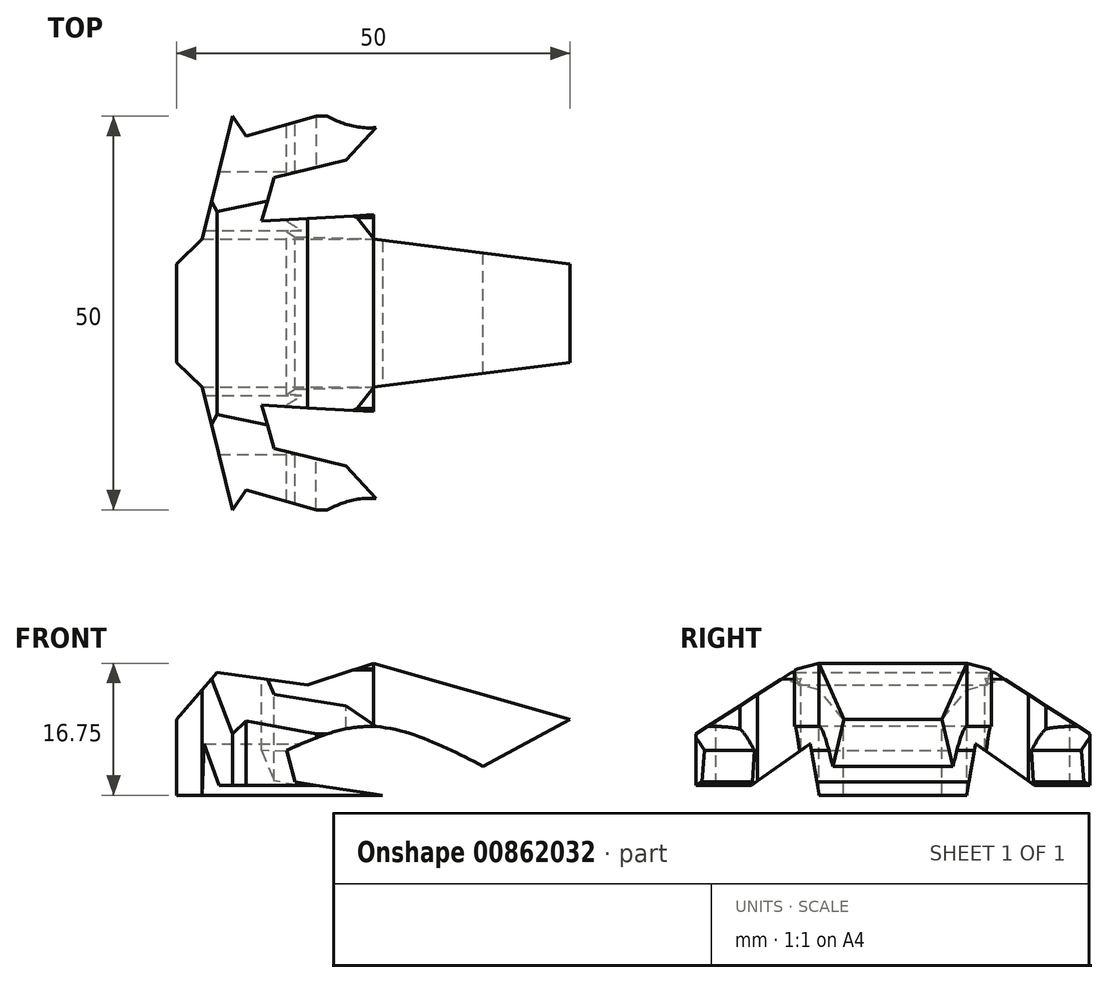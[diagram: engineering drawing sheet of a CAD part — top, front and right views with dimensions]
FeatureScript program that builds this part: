
annotation { "Feature Type Name" : "Feature", "Feature Type Description" : "" }
export const myFeature = defineFeature(function(context is Context, id is Id, definition is map)
    precondition{}
    {
        {
            var Q0;
            Q0=qCreatedBy(makeId("Top.planeOp"),FACE);
            var sketch = newSketch(context, id + "F0", { "sketchPlane" : qUnion([Q0])});
            skLineSegment(sketch, "E0.bottom", {"start": v(25, -25) * mm, "end": v(-25, -25) * mm});
            skLineSegment(sketch, "E0.top", {"start": v(25, 25) * mm, "end": v(-25, 25) * mm});
            skLineSegment(sketch, "E0.left", {"start": v(25, -25) * mm, "end": v(25, 25) * mm});
            skLineSegment(sketch, "E0.right", {"start": v(-25, -25) * mm, "end": v(-25, 25) * mm});
            skPoint(sketch, "E0.middle", {"position": v(0, 0) * mm});
            skSolve(sketch);
        }
        {
            var Q0;
            Q0=makeQuery(id+"F0.imprint","IMPRINT",FACE,{"disambiguationData":[TD([[makeQuery(id+"F0.imprint","IMPRINT",EDGE,{"derivedFrom":sQuery(id+"F0.wireOp",EDGE,"E0.bottom")}),-1.0]])]});
            extrude(context, id + "F1", {"entities" : qUnion([Q0]), "depth" : 50 * mm, "offsetDistance" : 25 * mm});
        }
        {
            var Q0;
            Q0=makeQuery(id+"F1.opExtrude","SWEPT_FACE",FACE,{"disambiguationData":[OSD([sQuery(id+"F0.wireOp",EDGE,"E0.top")])]});
            var sketch = newSketch(context, id + "F2", { "sketchPlane" : qUnion([Q0])});
            skLineSegment(sketch, "E1", {"start": v(-25, 25) * mm, "end": v(0, 32.14) * mm});
            skPoint(sketch, "E2", {"position": v(0, 0) * mm});
            skFitSpline(sketch, "E3", {"points": [v(-13.92, 19.08) * mm, v(0, 24.12) * mm, v(11, 21.1) * mm], "startDerivative": vector(26.84, 13.7) * mm, "endDerivative": vector(22.91, -10.19) * mm});
            skLineSegment(sketch, "E4", {"start": v(-25, 25) * mm, "end": v(-13.92, 19.08) * mm});
            skLineSegment(sketch, "E5", {"start": v(0, 32.14) * mm, "end": v(8.38, 29.43) * mm});
            skLineSegment(sketch, "E6", {"start": v(8.38, 29.43) * mm, "end": v(19.86, 30.97) * mm});
            skLineSegment(sketch, "E7", {"start": v(11, 21.1) * mm, "end": v(9.92, 17.07) * mm});
            skLineSegment(sketch, "E8", {"start": v(9.92, 17.07) * mm, "end": v(-1.63, 15.32) * mm});
            skLineSegment(sketch, "E9", {"start": v(-1.63, 15.32) * mm, "end": v(25, 15.32) * mm});
            skLineSegment(sketch, "E10", {"start": v(25, 15.32) * mm, "end": v(25, 25) * mm});
            skLineSegment(sketch, "E11", {"start": v(25, 25) * mm, "end": v(19.86, 30.97) * mm});
            skSolve(sketch);
        }
        {
            var Q0;
            Q0=makeQuery(id+"F1.opExtrude","SWEPT_FACE",FACE,{"disambiguationData":[OSD([sQuery(id+"F0.wireOp",EDGE,"E0.left")])]});
            var sketch = newSketch(context, id + "F3", { "sketchPlane" : qUnion([Q0])});
            skLineSegment(sketch, "E12", {"start": v(-25, 23.18) * mm, "end": v(-10.92, 26.77) * mm});
            skLineSegment(sketch, "E13", {"start": v(-25, 16.67) * mm, "end": v(-17.95, 16.67) * mm});
            skLineSegment(sketch, "E14", {"start": v(-17.95, 16.67) * mm, "end": v(-10.5, 21.93) * mm});
            skLineSegment(sketch, "E15", {"start": v(-10.5, 21.93) * mm, "end": v(-9.38, 15.39) * mm});
            skLineSegment(sketch, "E16", {"start": v(-9.38, 15.39) * mm, "end": v(0, 15.39) * mm});
            skLineSegment(sketch, "E17", {"start": v(-10.92, 26.77) * mm, "end": v(-12.11, 31.46) * mm});
            skLineSegment(sketch, "E18", {"start": v(-12.11, 31.46) * mm, "end": v(-6.5, 32.9) * mm});
            skLineSegment(sketch, "E19", {"start": v(-25, 23.18) * mm, "end": v(-12.11, 31.46) * mm});
            skLineSegment(sketch, "E20", {"start": v(-10.92, 26.77) * mm, "end": v(0, 32.9) * mm});
            skLineSegment(sketch, "E21", {"start": v(0, 32.9) * mm, "end": v(-6.5, 32.9) * mm});
            skLineSegment(sketch, "E22.MirrorCS", {"start": v(0, 32.9) * mm, "end": v(6.5, 32.9) * mm});
            skLineSegment(sketch, "E23.MirrorCS", {"start": v(12.11, 31.46) * mm, "end": v(6.5, 32.9) * mm});
            skLineSegment(sketch, "E24.MirrorCS", {"start": v(10.92, 26.77) * mm, "end": v(0, 32.9) * mm});
            skLineSegment(sketch, "E25.MirrorCS", {"start": v(10.92, 26.77) * mm, "end": v(12.11, 31.46) * mm});
            skLineSegment(sketch, "E26.MirrorCS", {"start": v(25, 23.18) * mm, "end": v(12.11, 31.46) * mm});
            skLineSegment(sketch, "E27.MirrorCS", {"start": v(25, 23.18) * mm, "end": v(10.92, 26.77) * mm});
            skLineSegment(sketch, "E28.MirrorCS", {"start": v(17.95, 16.67) * mm, "end": v(10.5, 21.93) * mm});
            skLineSegment(sketch, "E29.MirrorCS", {"start": v(25, 16.67) * mm, "end": v(17.95, 16.67) * mm});
            skLineSegment(sketch, "E30.MirrorCS", {"start": v(10.5, 21.93) * mm, "end": v(9.38, 15.39) * mm});
            skLineSegment(sketch, "E31.MirrorCS", {"start": v(9.38, 15.39) * mm, "end": v(0, 15.39) * mm});
            skLineSegment(sketch, "E32", {"start": v(-25, 23.18) * mm, "end": v(-25, 16.67) * mm});
            skLineSegment(sketch, "E33", {"start": v(25, 23.18) * mm, "end": v(25, 16.67) * mm});
            skLineSegment(sketch, "E34", {"start": v(-5.46, 29.83) * mm, "end": v(5.46, 29.83) * mm});
            skSolve(sketch);
        }
        {
            var Q0;
            Q0=makeQuery(id+"F1.opExtrude","CAP_FACE",FACE,{"disambiguationData":[OSD([sQuery(id+"F0.wireOp",EDGE,"E0.bottom"),sQuery(id+"F0.wireOp",EDGE,"E0.top"),sQuery(id+"F0.wireOp",EDGE,"E0.left"),sQuery(id+"F0.wireOp",EDGE,"E0.right")])],"isStart":false});
            var sketch = newSketch(context, id + "F4", { "sketchPlane" : qUnion([Q0])});
            skLineSegment(sketch, "E35", {"start": v(0, -9.38) * mm, "end": v(25, -6.25) * mm});
            skLineSegment(sketch, "E36", {"start": v(0, 9.38) * mm, "end": v(25, 6.25) * mm});
            skLineSegment(sketch, "E37", {"start": v(-17.85, -25) * mm, "end": v(-21.77, -9.37) * mm});
            skLineSegment(sketch, "E38", {"start": v(-25, 0) * mm, "end": v(25, 0) * mm});
            skLineSegment(sketch, "E39", {"start": v(-12.58, -17.21) * mm, "end": v(-14.18, -11.7) * mm});
            skLineSegment(sketch, "E40", {"start": v(-14.18, -11.7) * mm, "end": v(0, -12.5) * mm});
            skLineSegment(sketch, "E41", {"start": v(-16.14, -22.48) * mm, "end": v(-7.23, -25) * mm});
            skLineSegment(sketch, "E42", {"start": v(-7.23, -25) * mm, "end": v(1.64, -25) * mm});
            skLineSegment(sketch, "E43", {"start": v(-12.58, -17.21) * mm, "end": v(-3.47, -19.45) * mm});
            skLineSegment(sketch, "E44", {"start": v(-3.47, -19.45) * mm, "end": v(1.64, -25) * mm});
            skLineSegment(sketch, "E45.MirrorCS", {"start": v(-17.85, 25) * mm, "end": v(-21.77, 9.37) * mm});
            skLineSegment(sketch, "E46.MirrorCS", {"start": v(-12.58, 17.21) * mm, "end": v(-14.18, 11.7) * mm});
            skLineSegment(sketch, "E47.MirrorCS", {"start": v(-14.18, 11.7) * mm, "end": v(0, 12.5) * mm});
            skLineSegment(sketch, "E48.MirrorCS", {"start": v(-12.58, 17.21) * mm, "end": v(-3.47, 19.45) * mm});
            skLineSegment(sketch, "E49.MirrorCS", {"start": v(-16.14, 22.48) * mm, "end": v(-7.23, 25) * mm});
            skLineSegment(sketch, "E50.MirrorCS", {"start": v(-3.47, 19.45) * mm, "end": v(1.64, 25) * mm});
            skLineSegment(sketch, "E51.MirrorCS", {"start": v(-7.23, 25) * mm, "end": v(1.64, 25) * mm});
            skLineSegment(sketch, "E52", {"start": v(-21.77, -9.37) * mm, "end": v(-25, -6.25) * mm});
            skLineSegment(sketch, "E53", {"start": v(-25, -6.25) * mm, "end": v(-25, 0) * mm});
            skLineSegment(sketch, "E54.MirrorCS", {"start": v(-25, 6.25) * mm, "end": v(-25, 0) * mm});
            skLineSegment(sketch, "E55.MirrorCS", {"start": v(-21.77, 9.37) * mm, "end": v(-25, 6.25) * mm});
            skLineSegment(sketch, "E56", {"start": v(0, -12.5) * mm, "end": v(0, -9.38) * mm});
            skLineSegment(sketch, "E57", {"start": v(0, 9.38) * mm, "end": v(0, 12.5) * mm});
            skLineSegment(sketch, "E58", {"start": v(-17.85, -25) * mm, "end": v(-16.14, -22.48) * mm});
            skLineSegment(sketch, "E59", {"start": v(-17.85, 25) * mm, "end": v(-16.14, 22.48) * mm});
            skLineSegment(sketch, "E60", {"start": v(25, -6.25) * mm, "end": v(25, 6.25) * mm});
            skSolve(sketch);
        }
        {
            var Q0;
            {var subQ0=sQuery(id+"F4.wireOp",EDGE,"E37");Q0=makeQuery(id+"F4.imprint","IMPRINT",FACE,{"disambiguationData":[TD([[makeQuery(id+"F4.imprint","IMPRINT",EDGE,{"derivedFrom":subQ0}),1.0]])]});}
            var Q1;
            {var subQ0=sQuery(id+"F4.wireOp",EDGE,"E41");Q1=makeQuery(id+"F4.imprint","IMPRINT",FACE,{"disambiguationData":[TD([[makeQuery(id+"F4.imprint","IMPRINT",EDGE,{"derivedFrom":subQ0}),-1.0]])]});}
            var Q2;
            {var subQ0=sQuery(id+"F4.wireOp",EDGE,"E45.MirrorCS");Q2=makeQuery(id+"F4.imprint","IMPRINT",FACE,{"disambiguationData":[TD([[makeQuery(id+"F4.imprint","IMPRINT",EDGE,{"derivedFrom":subQ0}),-1.0]])]});}
            var Q3;
            {var subQ0=sQuery(id+"F4.wireOp",EDGE,"E49.MirrorCS");Q3=makeQuery(id+"F4.imprint","IMPRINT",FACE,{"disambiguationData":[TD([[makeQuery(id+"F4.imprint","IMPRINT",EDGE,{"derivedFrom":subQ0}),1.0]])]});}
            var Q4;
            {var subQ0=sQuery(id+"F4.wireOp",EDGE,"E36");Q4=makeQuery(id+"F4.imprint","IMPRINT",FACE,{"disambiguationData":[TD([[makeQuery(id+"F4.imprint","IMPRINT",EDGE,{"derivedFrom":subQ0}),1.0]])]});}
            var Q5;
            {var subQ4=sQuery(id+"F4.wireOp",EDGE,"E35");Q5=makeQuery(id+"F4.imprint","IMPRINT",FACE,{"disambiguationData":[TD([[makeQuery(id+"F4.imprint","IMPRINT",EDGE,{"derivedFrom":subQ4}),-1.0]])]});}
            extrude(context, id + "F5", {"entities" : qUnion([Q0, Q1, Q2, Q3, Q4, Q5]), "operationType" : NewBodyOperationType.REMOVE, "oppositeDirection" : true, "depth" : 50 * mm, "offsetDistance" : 25 * mm});
        }
        {
            var Q0;
            {var subQ4=sQuery(id+"F2.wireOp",EDGE,"E1");Q0=makeQuery(id+"F2.imprint","IMPRINT",FACE,{"disambiguationData":[TD([[makeQuery(id+"F2.imprint","IMPRINT",EDGE,{"derivedFrom":subQ4}),1.0]])]});}
            var Q1;
            Q1=makeQuery(id+"F2.imprint","IMPRINT",FACE,{"disambiguationData":[TD([[makeQuery(id+"F2.imprint","IMPRINT",EDGE,{"derivedFrom":sQuery(id+"F2.wireOp",EDGE,"E3")}),-1.0]])]});
            extrude(context, id + "F6", {"entities" : qUnion([Q0, Q1]), "operationType" : NewBodyOperationType.REMOVE, "oppositeDirection" : true, "depth" : 50 * mm, "offsetDistance" : 25 * mm});
        }
        {
            var Q0;
            Q0=makeQuery(id+"F3.imprint","IMPRINT",FACE,{"disambiguationData":[TD([[makeQuery(id+"F3.imprint","IMPRINT",EDGE,{"derivedFrom":sQuery(id+"F3.wireOp",EDGE,"E18")}),1.0]])]});
            var Q1;
            {var subQ3=sQuery(id+"F3.wireOp",EDGE,"E13");Q1=makeQuery(id+"F3.imprint","IMPRINT",FACE,{"disambiguationData":[TD([[makeQuery(id+"F3.imprint","IMPRINT",EDGE,{"derivedFrom":subQ3}),-1.0]])]});}
            extrude(context, id + "F7", {"entities" : qUnion([Q0, Q1]), "operationType" : NewBodyOperationType.REMOVE, "oppositeDirection" : true, "depth" : 50 * mm, "offsetDistance" : 25 * mm});
        }
    });
